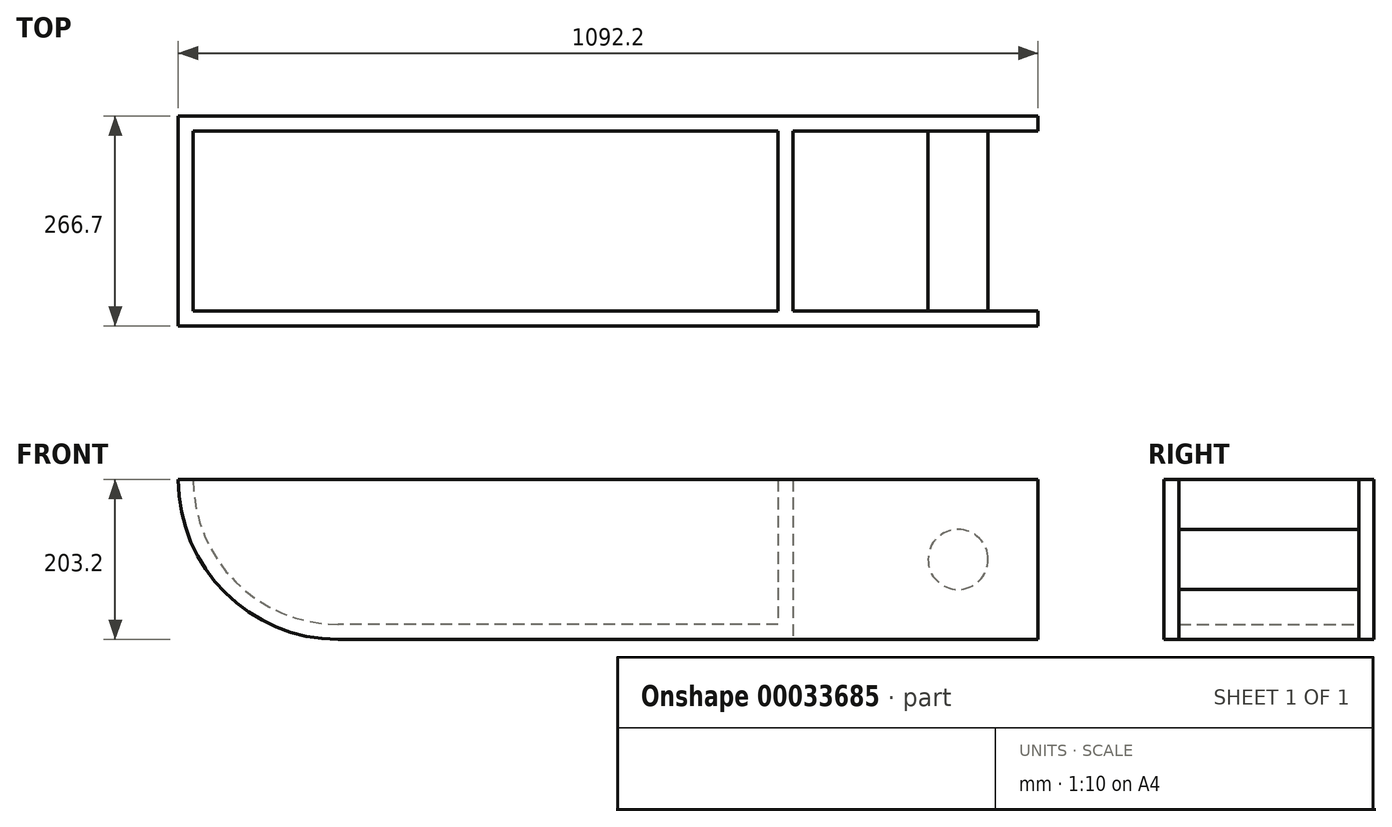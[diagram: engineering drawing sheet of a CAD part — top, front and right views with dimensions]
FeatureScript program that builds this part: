
annotation { "Feature Type Name" : "Feature", "Feature Type Description" : "" }
export const myFeature = defineFeature(function(context is Context, id is Id, definition is map)
    precondition{}
    {
        {
            var Q0;
            Q0=qCreatedBy(makeId("Front.planeOp"),FACE);
            var sketch = newSketch(context, id + "F0", { "sketchPlane" : qUnion([Q0])});
            skLineSegment(sketch, "E0.bottom", {"start": v(0, 0) * mm, "end": v(-635, 0) * mm});
            skLineSegment(sketch, "E0.top", {"start": v(0, -203.2) * mm, "end": v(-635, -203.2) * mm});
            skLineSegment(sketch, "E0.left", {"start": v(0, 0) * mm, "end": v(0, -203.2) * mm});
            skLineSegment(sketch, "E0.right", {"start": v(-635, 0) * mm, "end": v(-635, -203.2) * mm});
            skCircle(sketch, "E1", {"center": v(-635, 0) * mm, "radius": 203.2 * mm});
            skLineSegment(sketch, "E2", {"start": v(-635, 0) * mm, "end": v(-838.2, 0) * mm});
            skLineSegment(sketch, "E3.bottom", {"start": v(0, 0) * mm, "end": v(254, 0) * mm});
            skLineSegment(sketch, "E3.top", {"start": v(0, -203.2) * mm, "end": v(254, -203.2) * mm});
            skLineSegment(sketch, "E3.right", {"start": v(254, 0) * mm, "end": v(254, -203.2) * mm});
            skSolve(sketch);
        }
        {
            var Q0;
            {var subQ1=sQuery(id+"F0.wireOp",EDGE,"E0.top");Q0=makeQuery(id+"F0.imprint","IMPRINT",FACE,{"disambiguationData":[TD([[makeQuery(id+"F0.imprint","IMPRINT",EDGE,{"derivedFrom":subQ1}),-1.0]])]});}
            var Q1;
            {var subQ2=sQuery(id+"F0.wireOp",EDGE,"E0.right");Q1=makeQuery(id+"F0.imprint","IMPRINT",FACE,{"disambiguationData":[TD([[makeQuery(id+"F0.imprint","IMPRINT",EDGE,{"derivedFrom":subQ2}),-1.0]])]});}
            var Q2;
            {var subQ3=sQuery(id+"F0.wireOp",EDGE,"E0.right");Q2=makeQuery(id+"F0.imprint","IMPRINT",FACE,{"disambiguationData":[TD([[makeQuery(id+"F0.imprint","IMPRINT",EDGE,{"derivedFrom":subQ3}),1.0]])]});}
            var Q3;
            Q3=makeQuery(id+"F0.imprint","IMPRINT",FACE,{"disambiguationData":[TD([[makeQuery(id+"F0.imprint","IMPRINT",EDGE,{"derivedFrom":sQuery(id+"F0.wireOp",EDGE,"E3.bottom")}),-1.0]])]});
            extrude(context, id + "F1", {"entities" : qUnion([Q0, Q1, Q2, Q3]), "depth" : 19.05 * mm});
        }
        {
            var Q0;
            Q0=makeQuery(id+"F1.opExtrude","CAP_FACE",FACE,{"disambiguationData":[OSD([sQuery(id+"F0.wireOp",EDGE,"E0.bottom"),sQuery(id+"F0.wireOp",EDGE,"E0.top"),sQuery(id+"F0.wireOp",EDGE,"E0.left"),sQuery(id+"F0.wireOp",EDGE,"E1"),sQuery(id+"F0.wireOp",EDGE,"E2")])],"isStart":false});
            var sketch = newSketch(context, id + "F2", { "sketchPlane" : qUnion([Q0])});
            skCircle(sketch, "E4", {"center": v(152.4, -101.6) * mm, "radius": 38.1 * mm});
            skLineSegment(sketch, "E5.bottom", {"start": v(-57.15, 0) * mm, "end": v(-76.2, 0) * mm});
            skLineSegment(sketch, "E5.top", {"start": v(-57.15, -203.2) * mm, "end": v(-76.2, -203.2) * mm});
            skLineSegment(sketch, "E5.left", {"start": v(-57.15, 0) * mm, "end": v(-57.15, -203.2) * mm});
            skLineSegment(sketch, "E5.right", {"start": v(-76.2, 0) * mm, "end": v(-76.2, -203.2) * mm});
            skLineSegment(sketch, "E6.bottom", {"start": v(-76.2, -203.2) * mm, "end": v(-635, -203.2) * mm});
            skLineSegment(sketch, "E6.top", {"start": v(-76.2, -184.15) * mm, "end": v(-635, -184.15) * mm});
            skLineSegment(sketch, "E6.left", {"start": v(-76.2, -203.2) * mm, "end": v(-76.2, -184.15) * mm});
            skLineSegment(sketch, "E6.right", {"start": v(-635, -203.2) * mm, "end": v(-635, -184.15) * mm});
            skCircle(sketch, "E7", {"center": v(-635, 0) * mm, "radius": 184.15 * mm});
            skSolve(sketch);
        }
        {
            var Q0;
            Q0=makeQuery(id+"F2.imprint","IMPRINT",FACE,{"disambiguationData":[TD([[makeQuery(id+"F2.imprint","IMPRINT",EDGE,{"derivedFrom":sQuery(id+"F2.wireOp",EDGE,"E4")}),1.0]])]});
            var Q1;
            Q1=makeQuery(id+"F2.imprint","IMPRINT",FACE,{"disambiguationData":[TD([[makeQuery(id+"F2.imprint","IMPRINT",EDGE,{"derivedFrom":sQuery(id+"F2.wireOp",EDGE,"E5.bottom")}),1.0]])]});
            var Q2;
            Q2=makeQuery(id+"F2.imprint","IMPRINT",FACE,{"disambiguationData":[TD([[makeQuery(id+"F2.imprint","IMPRINT",EDGE,{"derivedFrom":sQuery(id+"F2.wireOp",EDGE,"E6.bottom")}),-1.0]])]});
            var Q3;
            {var subQ4=sQuery(id+"F2.wireOp",EDGE,"E6.right");Q3=makeQuery(id+"F2.imprint","IMPRINT",FACE,{"disambiguationData":[TD([[makeQuery(id+"F2.imprint","IMPRINT",EDGE,{"derivedFrom":subQ4}),1.0]])]});}
            extrude(context, id + "F3", {"entities" : qUnion([Q0, Q1, Q2, Q3]), "operationType" : NewBodyOperationType.ADD, "depth" : 228.6 * mm});
        }
        {
            var Q0;
            Q0=makeQuery(id+"F3.opExtrude","CAP_FACE",FACE,{"disambiguationData":[OSD([sQuery(id+"F0.wireOp",EDGE,"E0.bottom"),sQuery(id+"F0.wireOp",EDGE,"E1"),sQuery(id+"F0.wireOp",EDGE,"E2"),sQuery(id+"F0.wireOp",EDGE,"E3.bottom"),sQuery(id+"F2.wireOp",EDGE,"E5.bottom"),sQuery(id+"F2.wireOp",EDGE,"E5.top"),sQuery(id+"F2.wireOp",EDGE,"E5.left"),sQuery(id+"F2.wireOp",EDGE,"E5.right"),sQuery(id+"F2.wireOp",EDGE,"E6.bottom"),sQuery(id+"F2.wireOp",EDGE,"E6.top"),sQuery(id+"F2.wireOp",EDGE,"E7")])],"isStart":false});
            var sketch = newSketch(context, id + "F4", { "sketchPlane" : qUnion([Q0])});
            skLineSegment(sketch, "E8.bottom", {"start": v(0, 0) * mm, "end": v(-635, 0) * mm});
            skLineSegment(sketch, "E8.top", {"start": v(0, -203.2) * mm, "end": v(-635, -203.2) * mm});
            skLineSegment(sketch, "E8.left", {"start": v(0, 0) * mm, "end": v(0, -203.2) * mm});
            skLineSegment(sketch, "E8.right", {"start": v(-635, 0) * mm, "end": v(-635, -203.2) * mm});
            skCircle(sketch, "E9", {"center": v(-635, 0) * mm, "radius": 203.2 * mm});
            skLineSegment(sketch, "E10", {"start": v(-635, 0) * mm, "end": v(-838.2, 0) * mm});
            skLineSegment(sketch, "E11.bottom", {"start": v(0, 0) * mm, "end": v(254, 0) * mm});
            skLineSegment(sketch, "E11.top", {"start": v(0, -203.2) * mm, "end": v(254, -203.2) * mm});
            skLineSegment(sketch, "E11.right", {"start": v(254, 0) * mm, "end": v(254, -203.2) * mm});
            skSolve(sketch);
        }
        {
            var Q0;
            Q0=makeQuery(id+"F4.imprint","IMPRINT",FACE,{"disambiguationData":[TD([[makeQuery(id+"F4.imprint","IMPRINT",EDGE,{"derivedFrom":sQuery(id+"F4.wireOp",EDGE,"E11.bottom")}),-1.0]])]});
            var Q1;
            {var subQ1=sQuery(id+"F4.wireOp",EDGE,"E8.left");Q1=makeQuery(id+"F4.imprint","IMPRINT",FACE,{"disambiguationData":[TD([[makeQuery(id+"F4.imprint","IMPRINT",EDGE,{"derivedFrom":subQ1}),-1.0]])]});}
            var Q2;
            {var subQ0=makeQuery(id+"F3.opExtrude","CAP_EDGE",EDGE,{"disambiguationData":[OSD([sQuery(id+"F2.wireOp",EDGE,"E7")])],"isStart":false});Q2=makeQuery(id+"F4.imprint","IMPRINT",FACE,{"disambiguationData":[TD([[makeQuery(id+"F4.imprint","IMPRINT",EDGE,{"derivedFrom":subQ0}),1.0]])]});}
            var Q3;
            {var subQ0=makeQuery(id+"F3.opExtrude","CAP_EDGE",EDGE,{"disambiguationData":[OSD([sQuery(id+"F2.wireOp",EDGE,"E7")])],"isStart":false});Q3=makeQuery(id+"F4.imprint","IMPRINT",FACE,{"disambiguationData":[TD([[makeQuery(id+"F4.imprint","IMPRINT",EDGE,{"derivedFrom":subQ0}),-1.0]])]});}
            var Q4;
            {var subQ0=makeQuery(id+"F3.opExtrude","CAP_EDGE",EDGE,{"disambiguationData":[OSD([sQuery(id+"F2.wireOp",EDGE,"E5.right")])],"isStart":false});Q4=makeQuery(id+"F4.imprint","IMPRINT",FACE,{"disambiguationData":[TD([[makeQuery(id+"F4.imprint","IMPRINT",EDGE,{"derivedFrom":subQ0}),-1.0]])]});}
            var Q5;
            {var subQ6=makeQuery(id+"F3.opExtrude","CAP_EDGE",EDGE,{"disambiguationData":[OSD([sQuery(id+"F2.wireOp",EDGE,"E5.left")])],"isStart":false});Q5=makeQuery(id+"F4.imprint","IMPRINT",FACE,{"disambiguationData":[TD([[makeQuery(id+"F4.imprint","IMPRINT",EDGE,{"derivedFrom":subQ6}),-1.0]])]});}
            var Q6;
            {var subQ0=makeQuery(id+"F3.opExtrude","CAP_EDGE",EDGE,{"disambiguationData":[OSD([sQuery(id+"F2.wireOp",EDGE,"E6.top")])],"isStart":false});var subQ1=sQuery(id+"F4.wireOp",EDGE,"E9");var subQ2=makeQuery(id+"F4.imprint","INTERSECT",VERTEX,{"derivedFrom":[subQ0,subQ1]});Q6=makeQuery(id+"F4.imprint","IMPRINT",FACE,{"disambiguationData":[TD([[makeQuery(id+"F4.imprint","IMPRINT",EDGE,{"disambiguationData":[TD([[subQ2,1.0]])],"derivedFrom":subQ1}),1.0]])]});}
            var Q7;
            {var subQ1=sQuery(id+"F4.wireOp",EDGE,"E9");var subQ5=sQuery(id+"F4.wireOp",EDGE,"E8.bottom");var subQ6=makeQuery(id+"F4.imprint","INTERSECT",VERTEX,{"derivedFrom":[subQ5,subQ1]});Q7=makeQuery(id+"F4.imprint","IMPRINT",FACE,{"disambiguationData":[TD([[makeQuery(id+"F4.imprint","IMPRINT",EDGE,{"disambiguationData":[TD([[subQ6,1.0]])],"derivedFrom":subQ1}),1.0]])]});}
            extrude(context, id + "F5", {"entities" : qUnion([Q0, Q1, Q2, Q3, Q4, Q5, Q6, Q7]), "operationType" : NewBodyOperationType.ADD, "depth" : 19.05 * mm});
        }
    });
